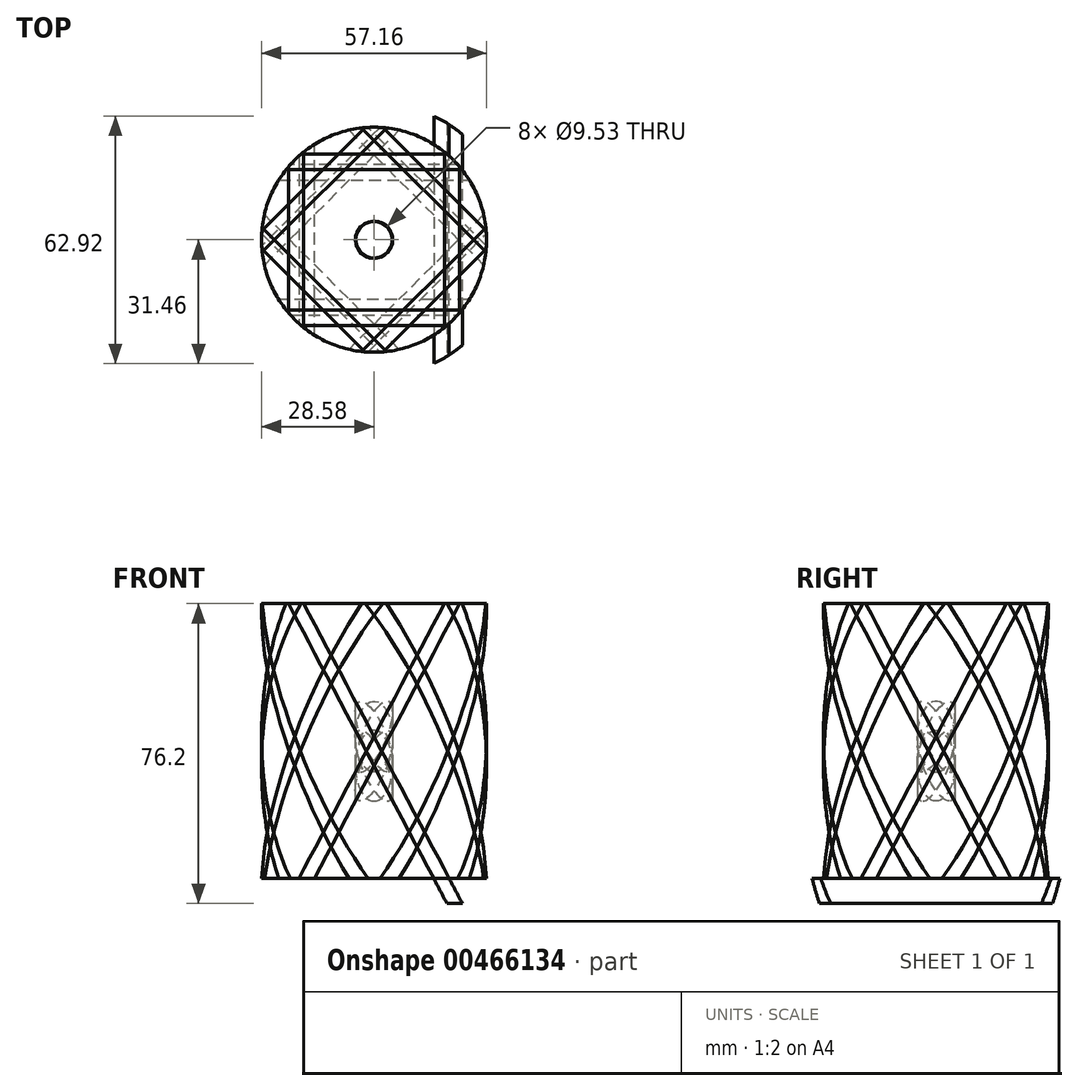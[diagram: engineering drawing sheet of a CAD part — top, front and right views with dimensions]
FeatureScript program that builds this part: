
annotation { "Feature Type Name" : "Feature", "Feature Type Description" : "" }
export const myFeature = defineFeature(function(context is Context, id is Id, definition is map)
    precondition{}
    {
        {
            var Q0;
            Q0=qCreatedBy(makeId("Top.planeOp"),FACE);
            var sketch = newSketch(context, id + "F0", { "sketchPlane" : qUnion([Q0])});
            skCircle(sketch, "E0", {"center": v(0, 0) * mm, "radius": 28.58 * mm});
            skCircle(sketch, "E1.0", {"center": v(0, 0) * mm, "radius": 22.22 * mm});
            skCircle(sketch, "E2", {"center": v(0, 0) * mm, "radius": 4.76 * mm});
            skCircle(sketch, "E3", {"center": v(0, 0) * mm, "radius": 34.93 * mm});
            skSolve(sketch);
        }
        {
            var Q0;
            Q0=qCreatedBy(makeId("Front.planeOp"),FACE);
            var sketch = newSketch(context, id + "F1", { "sketchPlane" : qUnion([Q0])});
            skLineSegment(sketch, "E4", {"start": v(-20.19, 74.24) * mm, "end": v(22.62, -6.7) * mm});
            skLineSegment(sketch, "E5", {"start": v(22.62, -6.7) * mm, "end": v(18.72, -6.7) * mm});
            skLineSegment(sketch, "E6", {"start": v(18.72, -6.7) * mm, "end": v(-24.1, 74.24) * mm});
            skLineSegment(sketch, "E7", {"start": v(-24.1, 74.24) * mm, "end": v(-20.19, 74.24) * mm});
            skLineSegment(sketch, "E8", {"start": v(0, 0) * mm, "end": v(0, 75.23) * mm, "construction": true});
            skSolve(sketch);
        }
        {
            var Q0;
            Q0=makeQuery(id+"F0.imprint","IMPRINT",FACE,{"disambiguationData":[TD([[makeQuery(id+"F0.imprint","IMPRINT",EDGE,{"derivedFrom":sQuery(id+"F0.wireOp",EDGE,"E0")}),-1.0]])]});
            var Q1;
            Q1=makeQuery(id+"F0.imprint","IMPRINT",FACE,{"disambiguationData":[TD([[makeQuery(id+"F0.imprint","IMPRINT",EDGE,{"derivedFrom":sQuery(id+"F0.wireOp",EDGE,"E0")}),1.0]])]});
            var Q2;
            Q2=makeQuery(id+"F0.imprint","IMPRINT",FACE,{"disambiguationData":[TD([[makeQuery(id+"F0.imprint","IMPRINT",EDGE,{"derivedFrom":sQuery(id+"F0.wireOp",EDGE,"E1.0")}),1.0]])]});
            extrude(context, id + "F2", {"entities" : qUnion([Q0, Q1, Q2]), "oppositeDirection" : true, "depth" : 6.35 * mm});
        }
        {
            var Q0;
            Q0=makeQuery(id+"F0.imprint","IMPRINT",FACE,{"disambiguationData":[TD([[makeQuery(id+"F0.imprint","IMPRINT",EDGE,{"derivedFrom":sQuery(id+"F0.wireOp",EDGE,"E1.0")}),1.0]])]});
            var Q1;
            Q1=makeQuery(id+"F0.imprint","IMPRINT",FACE,{"disambiguationData":[TD([[makeQuery(id+"F0.imprint","IMPRINT",EDGE,{"derivedFrom":sQuery(id+"F0.wireOp",EDGE,"E0")}),1.0]])]});
            extrude(context, id + "F3", {"entities" : qUnion([Q0, Q1]), "depth" : 69.85 * mm});
        }
        {
            var Q0;
            Q0 = qSketchRegion(id + "F1", true);
            extrude(context, id + "F4", {"entities" : qUnion([Q0]), "operationType" : NewBodyOperationType.INTERSECT, "depth" : 101.6 * mm, "symmetric" : true});
        }
        {
            var Q0;
            Q0=makeQuery(id+"F3.opExtrude","SWEPT_BODY",BODY,{"disambiguationData":[OSD([sQuery(id+"F0.wireOp",EDGE,"E0"),sQuery(id+"F0.wireOp",EDGE,"E2")])]});
            var Q1;
            Q1=sQuery(id+"F1.wireOp",EDGE,"E8");
            circularPattern(context, id + "F5", {"entities" : qUnion([Q0]), "axis" : qUnion([Q1]), "angle" : 360 * degree, "instanceCount" : 8, "equalSpace" : true});
        }
    });
